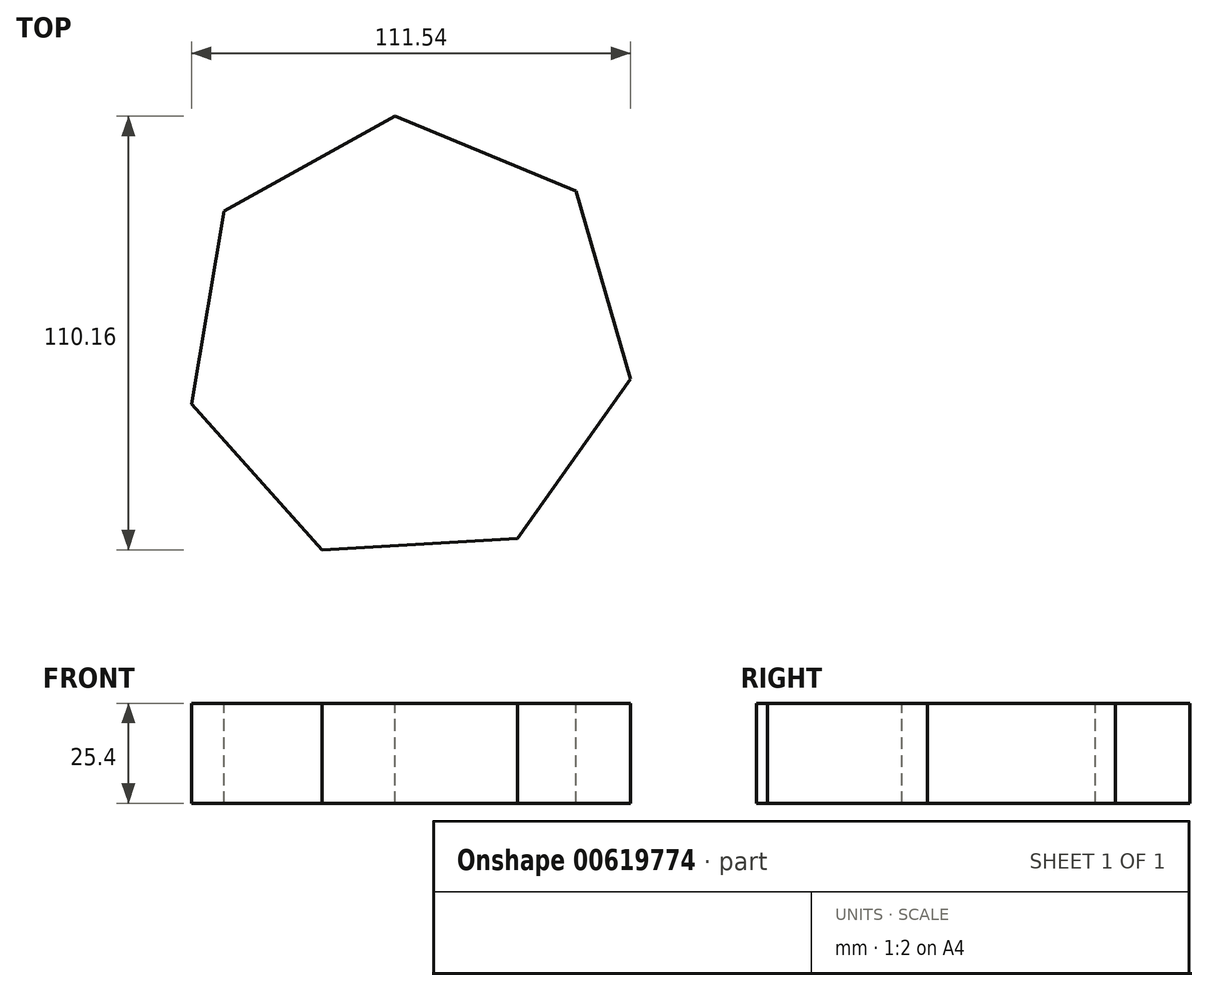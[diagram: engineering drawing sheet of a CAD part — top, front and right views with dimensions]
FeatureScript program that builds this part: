
annotation { "Feature Type Name" : "Feature", "Feature Type Description" : "" }
export const myFeature = defineFeature(function(context is Context, id is Id, definition is map)
    precondition{}
    {
        {
            var Q0;
            Q0=qCreatedBy(makeId("Top.planeOp"),FACE);
            var sketch = newSketch(context, id + "F0", { "sketchPlane" : qUnion([Q0])});
            skCircle(sketch, "E0.cCircle", {"center": v(0, 0) * mm, "radius": 51.62 * mm, "construction": true});
            skLineSegment(sketch, "E0.0", {"start": v(-55.04, -15.93) * mm, "end": v(-46.77, 33.1) * mm});
            skLineSegment(sketch, "E0.1", {"start": v(-46.77, 33.1) * mm, "end": v(-3.28, 57.2) * mm});
            skLineSegment(sketch, "E0.2", {"start": v(-3.28, 57.2) * mm, "end": v(42.68, 38.23) * mm});
            skLineSegment(sketch, "E0.3", {"start": v(42.68, 38.23) * mm, "end": v(56.5, -9.53) * mm});
            skLineSegment(sketch, "E0.4", {"start": v(56.5, -9.53) * mm, "end": v(27.78, -50.12) * mm});
            skLineSegment(sketch, "E0.5", {"start": v(27.78, -50.12) * mm, "end": v(-21.86, -52.96) * mm});
            skLineSegment(sketch, "E0.6", {"start": v(-21.86, -52.96) * mm, "end": v(-55.04, -15.93) * mm});
            skPoint(sketch, "E0.0.midPoint", {"position": v(-50.9, 8.59) * mm});
            skSolve(sketch);
        }
        {
            var Q0;
            Q0=makeQuery(id+"F0.imprint","IMPRINT",FACE,{"disambiguationData":[TD([[makeQuery(id+"F0.imprint","IMPRINT",EDGE,{"derivedFrom":sQuery(id+"F0.wireOp",EDGE,"E0.0")}),-1.0]])]});
            extrude(context, id + "F1", {"entities" : qUnion([Q0]), "oppositeDirection" : true, "depth" : 25.4 * mm, "offsetDistance" : 25.4 * mm});
        }
    });
